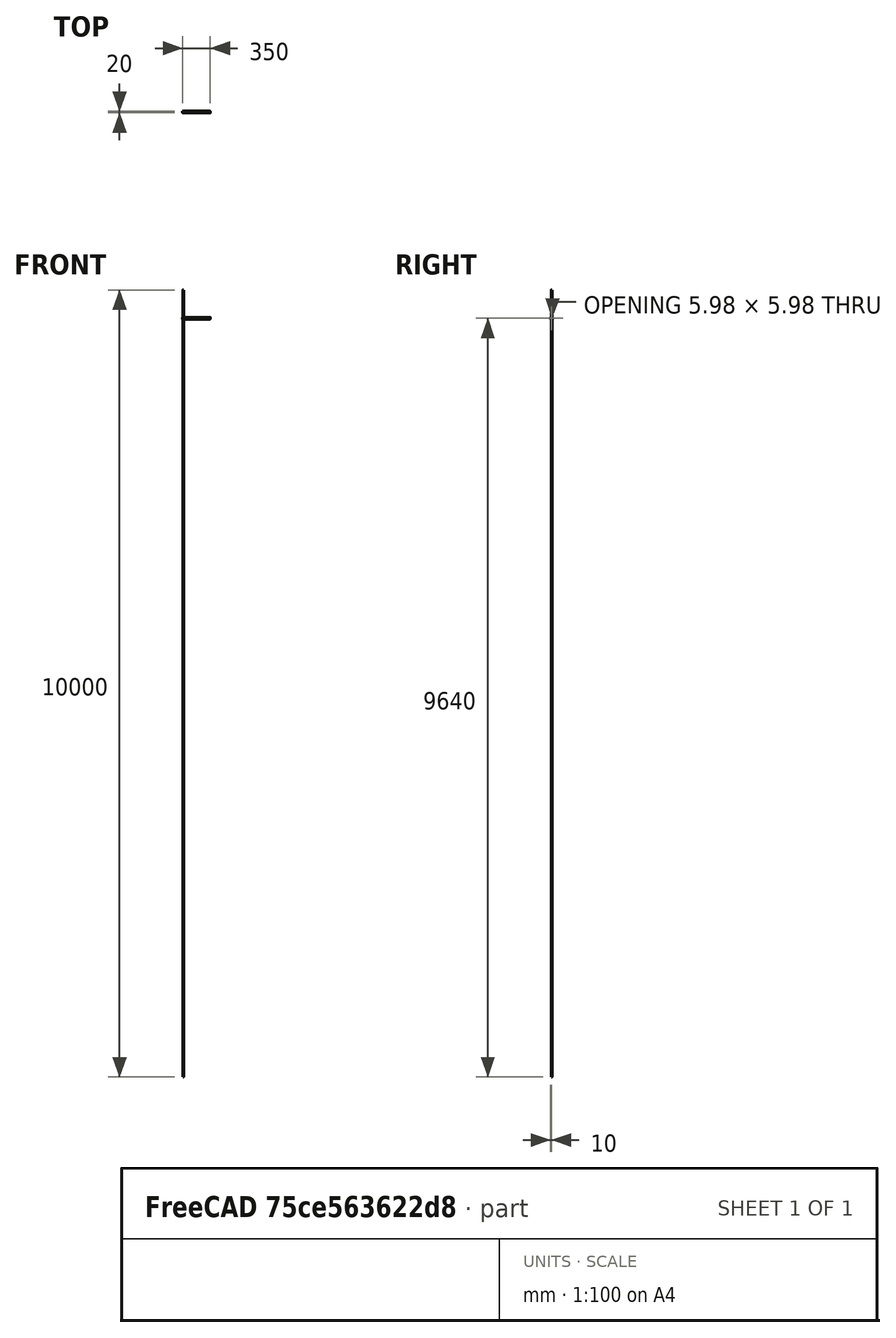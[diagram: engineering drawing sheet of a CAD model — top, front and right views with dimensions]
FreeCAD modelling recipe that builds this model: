
FCSTD DOCUMENT  (FreeCAD 0.14R3703 (Git))
Label: perfiles_horizontales_X
License: CC-BY 3.0
LicenseURL: http://creativecommons.org/licenses/by/3.0/
objects: Sketcher::SketchObject×2, PartDesign::Pad×1, PartDesign::Pocket×1, Part::Feature×1
note: 7 computed .brp shape members not serialized (recipe doc carries the construction recipe); baked Part::Feature solids carry a one-line shape summary decoded from their .brp

FEATURE [Sketcher::SketchObject] Sketch
  Placement = pos=(0,0,-1.5) rot=(0,1,0;1.5708rad)
  sketch-geometry (136):
    g0: LineSegment StartX=0 StartY=20 StartZ=0 EndX=4.65 EndY=20 EndZ=0
    g1: ArcOfCircle CenterX=-1e-12 CenterY=18.5 CenterZ=0 NormalX=0 NormalY=0 NormalZ=1 Radius=1.5 StartAngle=1.5708 EndAngle=3.14159
    g2: LineSegment StartX=-1.5 StartY=13.85 StartZ=0 EndX=-1.5 EndY=18.5 EndZ=0
    g3: ArcOfCircle CenterX=-1.3 CenterY=13.85 CenterZ=0 NormalX=0 NormalY=0 NormalZ=1 Radius=0.2 StartAngle=3.14159 EndAngle=4.71239
    g4: LineSegment StartX=-1 StartY=13.65 StartZ=0 EndX=-1.3 EndY=13.65 EndZ=0
    g5: LineSegment StartX=-1 StartY=13.3 StartZ=0 EndX=-1 EndY=13.65 EndZ=0
    g6: ArcOfCircle CenterX=-0.8 CenterY=13.3 CenterZ=0 NormalX=0 NormalY=0 NormalZ=1 Radius=0.2 StartAngle=3.14159 EndAngle=4.71239
    g7: LineSegment StartX=-0.5 StartY=13.1 StartZ=0 EndX=-0.8 EndY=13.1 EndZ=0
    g8: ArcOfCircle CenterX=-0.5 CenterY=13.6 CenterZ=0 NormalX=0 NormalY=0 NormalZ=1 Radius=0.5 StartAngle=4.71239 EndAngle=6.28319
    g9: LineSegment StartX=2.68e-07 StartY=15.5 StartZ=0 EndX=2.68e-07 EndY=13.6 EndZ=0
    g10: ArcOfCircle CenterX=0.5 CenterY=15.5 CenterZ=0 NormalX=0 NormalY=0 NormalZ=1 Radius=0.5 StartAngle=1.5708 EndAngle=3.14159
    g11: LineSegment StartX=1.23223 StartY=16 StartZ=0 EndX=0.5 EndY=16 EndZ=0
    g12: ArcOfCircle CenterX=1.23223 CenterY=15.5 CenterZ=0 NormalX=0 NormalY=0 NormalZ=1 Radius=0.5 StartAngle=0.785398 EndAngle=1.5708
    g13: LineSegment StartX=3.85355 StartY=13.5858 StartZ=0 EndX=1.58579 EndY=15.8536 EndZ=0
    g14: ArcOfCircle CenterX=3.5 CenterY=13.2322 CenterZ=0 NormalX=0 NormalY=0 NormalZ=1 Radius=0.5 StartAngle=0 EndAngle=0.785398
    g15: LineSegment StartX=4 StartY=10.9536 StartZ=0 EndX=4 EndY=13.2322 EndZ=0
    g16: ArcOfCircle CenterX=4.2 CenterY=10.9536 CenterZ=0 NormalX=0 NormalY=0 NormalZ=1 Radius=0.2 StartAngle=3.14159 EndAngle=3.66519
    g17: LineSegment StartX=4.46188 StartY=10.1 StartZ=0 EndX=4.0268 EndY=10.8536 EndZ=0
    g18: ArcOfCircle CenterX=4.28868 CenterY=10 CenterZ=0 NormalX=0 NormalY=0 NormalZ=1 Radius=0.2 StartAngle=5.75959 EndAngle=6.80678
    g19: LineSegment StartX=4.0268 StartY=9.14641 StartZ=0 EndX=4.46188 EndY=9.9 EndZ=0
    g20: ArcOfCircle CenterX=4.2 CenterY=9.04641 CenterZ=0 NormalX=0 NormalY=0 NormalZ=1 Radius=0.2 StartAngle=2.61799 EndAngle=3.14159
    g21: LineSegment StartX=4 StartY=6.76777 StartZ=0 EndX=4 EndY=9.04641 EndZ=0
    g22: ArcOfCircle CenterX=3.5 CenterY=6.76777 CenterZ=0 NormalX=0 NormalY=0 NormalZ=1 Radius=0.5 StartAngle=5.49779 EndAngle=6.28319
    g23: LineSegment StartX=1.58579 StartY=4.14645 StartZ=0 EndX=3.85355 EndY=6.41421 EndZ=0
    g24: ArcOfCircle CenterX=1.23223 CenterY=4.5 CenterZ=0 NormalX=0 NormalY=0 NormalZ=1 Radius=0.5 StartAngle=4.71239 EndAngle=5.49779
    g25: LineSegment StartX=0.5 StartY=4 StartZ=0 EndX=1.23223 EndY=4 EndZ=0
    g26: ArcOfCircle CenterX=0.5 CenterY=4.5 CenterZ=0 NormalX=0 NormalY=0 NormalZ=1 Radius=0.5 StartAngle=3.14159 EndAngle=4.71239
    g27: LineSegment StartX=2.68e-07 StartY=6.4 StartZ=0 EndX=2.68e-07 EndY=4.5 EndZ=0
    g28: ArcOfCircle CenterX=-0.5 CenterY=6.4 CenterZ=0 NormalX=0 NormalY=0 NormalZ=1 Radius=0.5 StartAngle=0 EndAngle=1.5708
    g29: LineSegment StartX=-0.8 StartY=6.9 StartZ=0 EndX=-0.5 EndY=6.9 EndZ=0
    g30: ArcOfCircle CenterX=-0.8 CenterY=6.7 CenterZ=0 NormalX=0 NormalY=0 NormalZ=1 Radius=0.2 StartAngle=1.5708 EndAngle=3.14159
    g31: LineSegment StartX=-1 StartY=6.35 StartZ=0 EndX=-1 EndY=6.7 EndZ=0
    g32: LineSegment StartX=-1.3 StartY=6.35 StartZ=0 EndX=-1 EndY=6.35 EndZ=0
    g33: ArcOfCircle CenterX=-1.3 CenterY=6.15 CenterZ=0 NormalX=0 NormalY=0 NormalZ=1 Radius=0.2 StartAngle=1.5708 EndAngle=3.14159
    g34: LineSegment StartX=-1.5 StartY=1.5 StartZ=0 EndX=-1.5 EndY=6.15 EndZ=0
    g35: ArcOfCircle CenterX=0 CenterY=1.5 CenterZ=0 NormalX=0 NormalY=0 NormalZ=1 Radius=1.5 StartAngle=3.14159 EndAngle=4.71239
    g36: LineSegment StartX=4.65 StartY=1e-12 StartZ=0 EndX=0 EndY=0 EndZ=0
    g37: ArcOfCircle CenterX=4.65 CenterY=0.2 CenterZ=0 NormalX=0 NormalY=0 NormalZ=1 Radius=0.2 StartAngle=4.71239 EndAngle=6.28319
    g38: LineSegment StartX=4.85 StartY=0.5 StartZ=0 EndX=4.85 EndY=0.2 EndZ=0
    g39: LineSegment StartX=5.2 StartY=0.5 StartZ=0 EndX=4.85 EndY=0.5 EndZ=0
    g40: ArcOfCircle CenterX=5.2 CenterY=0.7 CenterZ=0 NormalX=0 NormalY=0 NormalZ=1 Radius=0.2 StartAngle=4.71239 EndAngle=6.28319
    g41: LineSegment StartX=5.4 StartY=1 StartZ=0 EndX=5.4 EndY=0.7 EndZ=0
    g42: ArcOfCircle CenterX=4.9 CenterY=1 CenterZ=0 NormalX=0 NormalY=0 NormalZ=1 Radius=0.5 StartAngle=0 EndAngle=1.5708
    g43: LineSegment StartX=3 StartY=1.5 StartZ=0 EndX=4.9 EndY=1.5 EndZ=0
    g44: ArcOfCircle CenterX=3 CenterY=2 CenterZ=0 NormalX=0 NormalY=0 NormalZ=1 Radius=0.5 StartAngle=3.14159 EndAngle=4.71239
    g45: LineSegment StartX=2.5 StartY=2.73223 StartZ=0 EndX=2.5 EndY=2 EndZ=0
    g46: ArcOfCircle CenterX=3 CenterY=2.73223 CenterZ=0 NormalX=0 NormalY=0 NormalZ=1 Radius=0.5 StartAngle=2.35619 EndAngle=3.14159
    g47: LineSegment StartX=4.91421 StartY=5.35355 StartZ=0 EndX=2.64645 EndY=3.08579 EndZ=0
    g48: ArcOfCircle CenterX=5.26777 CenterY=5 CenterZ=0 NormalX=0 NormalY=0 NormalZ=1 Radius=0.5 StartAngle=1.5708 EndAngle=2.35619
    g49: LineSegment StartX=7.54641 StartY=5.5 StartZ=0 EndX=5.26777 EndY=5.5 EndZ=0
    g50: ArcOfCircle CenterX=7.54641 CenterY=5.7 CenterZ=0 NormalX=0 NormalY=0 NormalZ=1 Radius=0.2 StartAngle=4.71239 EndAngle=5.23599
    g51: LineSegment StartX=8.4 StartY=5.96188 StartZ=0 EndX=7.64641 EndY=5.52679 EndZ=0
    g52: ArcOfCircle CenterX=8.5 CenterY=5.78868 CenterZ=0 NormalX=0 NormalY=0 NormalZ=1 Radius=0.2 StartAngle=1.0472 EndAngle=2.0944
    g53: LineSegment StartX=9.35359 StartY=5.52679 StartZ=0 EndX=8.6 EndY=5.96188 EndZ=0
    g54: ArcOfCircle CenterX=9.45359 CenterY=5.7 CenterZ=0 NormalX=0 NormalY=0 NormalZ=1 Radius=0.2 StartAngle=4.18879 EndAngle=4.71239
    g55: LineSegment StartX=11.7322 StartY=5.5 StartZ=0 EndX=9.45359 EndY=5.5 EndZ=0
    g56: ArcOfCircle CenterX=11.7322 CenterY=5 CenterZ=0 NormalX=0 NormalY=0 NormalZ=1 Radius=0.5 StartAngle=0.785398 EndAngle=1.5708
    g57: LineSegment StartX=14.3536 StartY=3.08579 StartZ=0 EndX=12.0858 EndY=5.35355 EndZ=0
    g58: ArcOfCircle CenterX=14 CenterY=2.73223 CenterZ=0 NormalX=0 NormalY=0 NormalZ=1 Radius=0.5 StartAngle=0 EndAngle=0.785398
    g59: LineSegment StartX=14.5 StartY=2 StartZ=0 EndX=14.5 EndY=2.73223 EndZ=0
    g60: ArcOfCircle CenterX=14 CenterY=2 CenterZ=0 NormalX=0 NormalY=0 NormalZ=1 Radius=0.5 StartAngle=4.71239 EndAngle=6.28319
    g61: LineSegment StartX=12.1 StartY=1.5 StartZ=0 EndX=14 EndY=1.5 EndZ=0
    g62: ArcOfCircle CenterX=12.1 CenterY=1 CenterZ=0 NormalX=0 NormalY=0 NormalZ=1 Radius=0.5 StartAngle=1.5708 EndAngle=3.14159
    g63: LineSegment StartX=11.6 StartY=0.7 StartZ=0 EndX=11.6 EndY=1 EndZ=0
    g64: ArcOfCircle CenterX=11.8 CenterY=0.7 CenterZ=0 NormalX=0 NormalY=0 NormalZ=1 Radius=0.2 StartAngle=3.14159 EndAngle=4.71239
    g65: LineSegment StartX=12.15 StartY=0.5 StartZ=0 EndX=11.8 EndY=0.5 EndZ=0
    g66: LineSegment StartX=12.15 StartY=0.2 StartZ=0 EndX=12.15 EndY=0.5 EndZ=0
    g67: ArcOfCircle CenterX=12.35 CenterY=0.2 CenterZ=0 NormalX=0 NormalY=0 NormalZ=1 Radius=0.2 StartAngle=3.14159 EndAngle=4.71239
    g68: LineSegment StartX=17 StartY=1e-12 StartZ=0 EndX=12.35 EndY=0 EndZ=0
    g69: ArcOfCircle CenterX=17 CenterY=1.5 CenterZ=0 NormalX=0 NormalY=0 NormalZ=1 Radius=1.5 StartAngle=4.71239 EndAngle=6.28319
    g70: LineSegment StartX=18.5 StartY=6.15 StartZ=0 EndX=18.5 EndY=1.5 EndZ=0
    g71: ArcOfCircle CenterX=18.3 CenterY=6.15 CenterZ=0 NormalX=0 NormalY=0 NormalZ=1 Radius=0.2 StartAngle=0 EndAngle=1.5708
    g72: LineSegment StartX=18 StartY=6.35 StartZ=0 EndX=18.3 EndY=6.35 EndZ=0
    g73: LineSegment StartX=18 StartY=6.7 StartZ=0 EndX=18 EndY=6.35 EndZ=0
    g74: ArcOfCircle CenterX=17.8 CenterY=6.7 CenterZ=0 NormalX=0 NormalY=0 NormalZ=1 Radius=0.2 StartAngle=0 EndAngle=1.5708
    g75: LineSegment StartX=17.5 StartY=6.9 StartZ=0 EndX=17.8 EndY=6.9 EndZ=0
    g76: ArcOfCircle CenterX=17.5 CenterY=6.4 CenterZ=0 NormalX=0 NormalY=0 NormalZ=1 Radius=0.5 StartAngle=1.5708 EndAngle=3.14159
    g77: LineSegment StartX=17 StartY=4.5 StartZ=0 EndX=17 EndY=6.4 EndZ=0
    g78: ArcOfCircle CenterX=16.5 CenterY=4.5 CenterZ=0 NormalX=0 NormalY=0 NormalZ=1 Radius=0.5 StartAngle=4.71239 EndAngle=6.28319
    g79: LineSegment StartX=15.7678 StartY=4 StartZ=0 EndX=16.5 EndY=4 EndZ=0
    g80: ArcOfCircle CenterX=15.7678 CenterY=4.5 CenterZ=0 NormalX=0 NormalY=0 NormalZ=1 Radius=0.5 StartAngle=3.92699 EndAngle=4.71239
    g81: LineSegment StartX=13.1464 StartY=6.41421 StartZ=0 EndX=15.4142 EndY=4.14645 EndZ=0
    g82: ArcOfCircle CenterX=13.5 CenterY=6.76777 CenterZ=0 NormalX=0 NormalY=0 NormalZ=1 Radius=0.5 StartAngle=3.14159 EndAngle=3.92699
    g83: LineSegment StartX=13 StartY=9.04641 StartZ=0 EndX=13 EndY=6.76777 EndZ=0
    g84: ArcOfCircle CenterX=12.8 CenterY=9.04641 CenterZ=0 NormalX=0 NormalY=0 NormalZ=1 Radius=0.2 StartAngle=0 EndAngle=0.523599
    g85: LineSegment StartX=12.5381 StartY=9.9 StartZ=0 EndX=12.9732 EndY=9.14641 EndZ=0
    g86: ArcOfCircle CenterX=12.7113 CenterY=10 CenterZ=0 NormalX=0 NormalY=0 NormalZ=1 Radius=0.2 StartAngle=2.61799 EndAngle=3.66519
    g87: LineSegment StartX=12.9732 StartY=10.8536 StartZ=0 EndX=12.5381 EndY=10.1 EndZ=0
    g88: ArcOfCircle CenterX=12.8 CenterY=10.9536 CenterZ=0 NormalX=0 NormalY=0 NormalZ=1 Radius=0.2 StartAngle=5.75959 EndAngle=6.28319
    g89: LineSegment StartX=13 StartY=13.2322 StartZ=0 EndX=13 EndY=10.9536 EndZ=0
    g90: ArcOfCircle CenterX=13.5 CenterY=13.2322 CenterZ=0 NormalX=0 NormalY=0 NormalZ=1 Radius=0.5 StartAngle=2.35619 EndAngle=3.14159
    g91: LineSegment StartX=15.4142 StartY=15.8536 StartZ=0 EndX=13.1464 EndY=13.5858 EndZ=0
    g92: ArcOfCircle CenterX=15.7678 CenterY=15.5 CenterZ=0 NormalX=0 NormalY=0 NormalZ=1 Radius=0.5 StartAngle=1.5708 EndAngle=2.35619
    g93: LineSegment StartX=16.5 StartY=16 StartZ=0 EndX=15.7678 EndY=16 EndZ=0
    g94: ArcOfCircle CenterX=16.5 CenterY=15.5 CenterZ=0 NormalX=0 NormalY=0 NormalZ=1 Radius=0.5 StartAngle=0 EndAngle=1.5708
    g95: LineSegment StartX=17 StartY=13.6 StartZ=0 EndX=17 EndY=15.5 EndZ=0
    g96: ArcOfCircle CenterX=17.5 CenterY=13.6 CenterZ=0 NormalX=0 NormalY=0 NormalZ=1 Radius=0.5 StartAngle=3.14159 EndAngle=4.71239
    g97: LineSegment StartX=17.8 StartY=13.1 StartZ=0 EndX=17.5 EndY=13.1 EndZ=0
    g98: ArcOfCircle CenterX=17.8 CenterY=13.3 CenterZ=0 NormalX=0 NormalY=0 NormalZ=1 Radius=0.2 StartAngle=4.71239 EndAngle=6.28319
    g99: LineSegment StartX=18 StartY=13.65 StartZ=0 EndX=18 EndY=13.3 EndZ=0
    g100: LineSegment StartX=18.3 StartY=13.65 StartZ=0 EndX=18 EndY=13.65 EndZ=0
    g101: ArcOfCircle CenterX=18.3 CenterY=13.85 CenterZ=0 NormalX=0 NormalY=0 NormalZ=1 Radius=0.2 StartAngle=4.71239 EndAngle=6.28319
    g102: LineSegment StartX=18.5 StartY=18.5 StartZ=0 EndX=18.5 EndY=13.85 EndZ=0
    g103: ArcOfCircle CenterX=17 CenterY=18.5 CenterZ=0 NormalX=0 NormalY=0 NormalZ=1 Radius=1.5 StartAngle=0 EndAngle=1.5708
    g104: LineSegment StartX=12.35 StartY=20 StartZ=0 EndX=17 EndY=20 EndZ=0
    g105: ArcOfCircle CenterX=12.35 CenterY=19.8 CenterZ=0 NormalX=0 NormalY=0 NormalZ=1 Radius=0.2 StartAngle=1.5708 EndAngle=3.14159
    g106: LineSegment StartX=12.15 StartY=19.5 StartZ=0 EndX=12.15 EndY=19.8 EndZ=0
    g107: LineSegment StartX=11.8 StartY=19.5 StartZ=0 EndX=12.15 EndY=19.5 EndZ=0
    g108: ArcOfCircle CenterX=11.8 CenterY=19.3 CenterZ=0 NormalX=0 NormalY=0 NormalZ=1 Radius=0.2 StartAngle=1.5708 EndAngle=3.14159
    g109: LineSegment StartX=11.6 StartY=19 StartZ=0 EndX=11.6 EndY=19.3 EndZ=0
    g110: ArcOfCircle CenterX=12.1 CenterY=19 CenterZ=0 NormalX=0 NormalY=0 NormalZ=1 Radius=0.5 StartAngle=3.14159 EndAngle=4.71239
    g111: LineSegment StartX=14 StartY=18.5 StartZ=0 EndX=12.1 EndY=18.5 EndZ=0
    g112: ArcOfCircle CenterX=14 CenterY=18 CenterZ=0 NormalX=0 NormalY=0 NormalZ=1 Radius=0.5 StartAngle=0 EndAngle=1.5708
    g113: LineSegment StartX=14.5 StartY=17.2678 StartZ=0 EndX=14.5 EndY=18 EndZ=0
    g114: ArcOfCircle CenterX=14 CenterY=17.2678 CenterZ=0 NormalX=0 NormalY=0 NormalZ=1 Radius=0.5 StartAngle=5.49779 EndAngle=6.28319
    g115: LineSegment StartX=12.0858 StartY=14.6464 StartZ=0 EndX=14.3536 EndY=16.9142 EndZ=0
    g116: ArcOfCircle CenterX=11.7322 CenterY=15 CenterZ=0 NormalX=0 NormalY=0 NormalZ=1 Radius=0.5 StartAngle=4.71239 EndAngle=5.49779
    g117: LineSegment StartX=9.45359 StartY=14.5 StartZ=0 EndX=11.7322 EndY=14.5 EndZ=0
    g118: ArcOfCircle CenterX=9.45359 CenterY=14.3 CenterZ=0 NormalX=0 NormalY=0 NormalZ=1 Radius=0.2 StartAngle=1.5708 EndAngle=2.0944
    g119: LineSegment StartX=8.6 StartY=14.0381 StartZ=0 EndX=9.35359 EndY=14.4732 EndZ=0
    g120: ArcOfCircle CenterX=8.5 CenterY=14.2113 CenterZ=0 NormalX=0 NormalY=0 NormalZ=1 Radius=0.2 StartAngle=4.18879 EndAngle=5.23599
    g121: LineSegment StartX=7.64641 StartY=14.4732 StartZ=0 EndX=8.4 EndY=14.0381 EndZ=0
    g122: ArcOfCircle CenterX=7.54641 CenterY=14.3 CenterZ=0 NormalX=0 NormalY=0 NormalZ=1 Radius=0.2 StartAngle=1.0472 EndAngle=1.5708
    g123: LineSegment StartX=5.26777 StartY=14.5 StartZ=0 EndX=7.54641 EndY=14.5 EndZ=0
    g124: ArcOfCircle CenterX=5.26777 CenterY=15 CenterZ=0 NormalX=0 NormalY=0 NormalZ=1 Radius=0.5 StartAngle=3.92699 EndAngle=4.71239
    g125: LineSegment StartX=2.64645 StartY=16.9142 StartZ=0 EndX=4.91421 EndY=14.6464 EndZ=0
    g126: ArcOfCircle CenterX=3 CenterY=17.2678 CenterZ=0 NormalX=0 NormalY=0 NormalZ=1 Radius=0.5 StartAngle=3.14159 EndAngle=3.92699
    g127: LineSegment StartX=2.5 StartY=18 StartZ=0 EndX=2.5 EndY=17.2678 EndZ=0
    g128: ArcOfCircle CenterX=3 CenterY=18 CenterZ=0 NormalX=0 NormalY=0 NormalZ=1 Radius=0.5 StartAngle=1.5708 EndAngle=3.14159
    g129: LineSegment StartX=4.9 StartY=18.5 StartZ=0 EndX=3 EndY=18.5 EndZ=0
    g130: ArcOfCircle CenterX=4.9 CenterY=19 CenterZ=0 NormalX=0 NormalY=0 NormalZ=1 Radius=0.5 StartAngle=4.71239 EndAngle=6.28319
    g131: LineSegment StartX=5.4 StartY=19.3 StartZ=0 EndX=5.4 EndY=19 EndZ=0
    g132: ArcOfCircle CenterX=5.2 CenterY=19.3 CenterZ=0 NormalX=0 NormalY=0 NormalZ=1 Radius=0.2 StartAngle=0 EndAngle=1.5708
    g133: LineSegment StartX=4.85 StartY=19.5 StartZ=0 EndX=5.2 EndY=19.5 EndZ=0
    g134: LineSegment StartX=4.85 StartY=19.8 StartZ=0 EndX=4.85 EndY=19.5 EndZ=0
    g135: ArcOfCircle CenterX=4.65 CenterY=19.8 CenterZ=0 NormalX=0 NormalY=0 NormalZ=1 Radius=0.2 StartAngle=0 EndAngle=1.5708
  constraints (136):
    c: Coincident(g0,g1)
    c: Coincident(g135,g0)
    c: Coincident(g1,g2)
    c: Coincident(g2,g3)
    c: Coincident(g3,g4)
    c: Coincident(g4,g5)
    c: Coincident(g6,g5)
    c: Coincident(g7,g6)
    c: Coincident(g8,g7)
    c: Coincident(g9,g8)
    c: Coincident(g10,g9)
    c: Coincident(g10,g11)
    c: Coincident(g11,g12)
    c: Coincident(g12,g13)
    c: Coincident(g14,g13)
    c: Coincident(g15,g14)
    c: Coincident(g15,g16)
    c: Coincident(g16,g17)
    c: Coincident(g17,g18)
    c: Coincident(g18,g19)
    c: Coincident(g19,g20)
    c: Coincident(g20,g21)
    c: Coincident(g21,g22)
    c: Coincident(g22,g23)
    c: Coincident(g23,g24)
    c: Coincident(g24,g25)
    c: Coincident(g26,g25)
    c: Coincident(g26,g27)
    c: Coincident(g28,g27)
    c: Coincident(g28,g29)
    c: Coincident(g30,g29)
    c: Coincident(g31,g30)
    c: Coincident(g31,g32)
    c: Coincident(g32,g33)
    c: Coincident(g33,g34)
    c: Coincident(g35,g34)
    c: Coincident(g36,g35)
    c: Coincident(g37,g36)
    c: Coincident(g37,g38)
    c: Coincident(g38,g39)
    c: Coincident(g40,g39)
    c: Coincident(g40,g41)
    c: Coincident(g41,g42)
    c: Coincident(g43,g42)
    c: Coincident(g44,g43)
    c: Coincident(g44,g45)
    c: Coincident(g45,g46)
    c: Coincident(g46,g47)
    c: Coincident(g47,g48)
    c: Coincident(g49,g48)
    c: Coincident(g49,g50)
    c: Coincident(g50,g51)
    c: Coincident(g51,g52)
    c: Coincident(g53,g52)
    c: Coincident(g54,g53)
    c: Coincident(g55,g54)
    c: Coincident(g56,g55)
    c: Coincident(g56,g57)
    c: Coincident(g58,g57)
    c: Coincident(g59,g58)
    c: Coincident(g60,g59)
    c: Coincident(g61,g60)
    c: Coincident(g62,g61)
    c: Coincident(g62,g63)
    c: Coincident(g64,g63)
    c: Coincident(g65,g64)
    c: Coincident(g66,g65)
    c: Coincident(g67,g66)
    c: Coincident(g67,g68)
    c: Coincident(g69,g68)
    c: Coincident(g70,g69)
    c: Coincident(g71,g70)
    c: Coincident(g72,g71)
    c: Coincident(g73,g72)
    c: Coincident(g73,g74)
    c: Coincident(g75,g74)
    c: Coincident(g76,g75)
    c: Coincident(g76,g77)
    c: Coincident(g77,g78)
    c: Coincident(g78,g79)
    c: Coincident(g80,g79)
    c: Coincident(g81,g80)
    c: Coincident(g81,g82)
    c: Coincident(g82,g83)
    c: Coincident(g83,g84)
    c: Coincident(g85,g84)
    c: Coincident(g86,g85)
    c: Coincident(g86,g87)
    c: Coincident(g88,g87)
    c: Coincident(g88,g89)
    c: Coincident(g89,g90)
    c: Coincident(g91,g90)
    c: Coincident(g92,g91)
    c: Coincident(g93,g92)
    c: Coincident(g94,g93)
    c: Coincident(g94,g95)
    c: Coincident(g95,g96)
    c: Coincident(g96,g97)
    c: Coincident(g98,g97)
    c: Coincident(g98,g99)
    c: Coincident(g100,g99)
    c: Coincident(g100,g101)
    c: Coincident(g101,g102)
    c: Coincident(g102,g103)
    c: Coincident(g103,g104)
    c: Coincident(g104,g105)
    c: Coincident(g106,g105)
    c: Coincident(g107,g106)
    c: Coincident(g108,g107)
    c: Coincident(g109,g108)
    c: Coincident(g110,g109)
    c: Coincident(g111,g110)
    c: Coincident(g112,g111)
    c: Coincident(g112,g113)
    c: Coincident(g113,g114)
    c: Coincident(g114,g115)
    c: Coincident(g115,g116)
    c: Coincident(g117,g116)
    c: Coincident(g118,g117)
    c: Coincident(g119,g118)
    c: Coincident(g119,g120)
    c: Coincident(g121,g120)
    c: Coincident(g121,g122)
    c: Coincident(g122,g123)
    c: Coincident(g124,g123)
    c: Coincident(g124,g125)
    c: Coincident(g126,g125)
    c: Coincident(g127,g126)
    c: Coincident(g128,g127)
    c: Coincident(g129,g128)
    c: Coincident(g130,g129)
    c: Coincident(g130,g131)
    c: Coincident(g131,g132)
    c: Coincident(g133,g132)
    c: Coincident(g134,g133)
    c: Coincident(g135,g134)
FEATURE [PartDesign::Pad] Pad
  Length = 350
  Length2 = 100
  Placement = pos=(0,0,-1.5) rot=(0,1,0;1.5708rad)
  Sketch = -> Sketch
  Type = 0
FEATURE [Sketcher::SketchObject] Sketch001
  Placement = pos=(350,0,-1.5) rot=(0,1,0;1.5708rad)
  Support = -> Pad [Face138]
  sketch-geometry (16):
    g0: ArcOfCircle CenterX=8.5 CenterY=10 CenterZ=0 NormalX=0 NormalY=0 NormalZ=1 Radius=3.54978 StartAngle=2.14023 EndAngle=2.57348
    g1: LineSegment StartX=6.5861 StartY=12.9896 StartZ=0 EndX=7.24181 EndY=12.4453 EndZ=0
    g2: ArcOfCircle CenterX=8.5 CenterY=10 CenterZ=0 NormalX=0 NormalY=0 NormalZ=1 Radius=2.75 StartAngle=1.09559 EndAngle=2.046
    g3: LineSegment StartX=9.75819 StartY=12.4453 StartZ=0 EndX=10.4139 EndY=12.9896 EndZ=0
    g4: ArcOfCircle CenterX=8.5 CenterY=10 CenterZ=0 NormalX=0 NormalY=0 NormalZ=1 Radius=3.54978 StartAngle=0.568112 EndAngle=1.00136
    g5: LineSegment StartX=11.4922 StartY=11.9099 StartZ=0 EndX=10.9453 EndY=11.2582 EndZ=0
    g6: ArcOfCircle CenterX=8.5 CenterY=10 CenterZ=0 NormalX=0 NormalY=0 NormalZ=1 Radius=2.75 StartAngle=5.80798 EndAngle=6.75839
    g7: LineSegment StartX=10.9453 StartY=8.74181 StartZ=0 EndX=11.4922 EndY=8.09007 EndZ=0
    g8: ArcOfCircle CenterX=8.5 CenterY=10 CenterZ=0 NormalX=0 NormalY=0 NormalZ=1 Radius=3.54978 StartAngle=5.28183 EndAngle=5.71507
    g9: LineSegment StartX=10.4139 StartY=7.01036 StartZ=0 EndX=9.75819 EndY=7.5547 EndZ=0
    g10: ArcOfCircle CenterX=8.5 CenterY=10 CenterZ=0 NormalX=0 NormalY=0 NormalZ=1 Radius=2.75 StartAngle=4.23718 EndAngle=5.1876
    g11: LineSegment StartX=7.24181 StartY=7.5547 StartZ=0 EndX=6.5861 EndY=7.01036 EndZ=0
    g12: ArcOfCircle CenterX=8.5 CenterY=10 CenterZ=0 NormalX=0 NormalY=0 NormalZ=1 Radius=3.54978 StartAngle=3.7097 EndAngle=4.14295
    g13: LineSegment StartX=5.50783 StartY=8.09007 StartZ=0 EndX=6.0547 EndY=8.74181 EndZ=0
    g14: ArcOfCircle CenterX=8.5 CenterY=10 CenterZ=0 NormalX=0 NormalY=0 NormalZ=1 Radius=2.75 StartAngle=2.66639 EndAngle=3.6168
    g15: LineSegment StartX=6.0547 StartY=11.2582 StartZ=0 EndX=5.50783 EndY=11.9099 EndZ=0
  constraints (16):
    c: Coincident(g0,g1)
    c: Coincident(g15,g0)
    c: Coincident(g1,g2)
    c: Coincident(g3,g2)
    c: Coincident(g4,g3)
    c: Coincident(g4,g5)
    c: Coincident(g6,g5)
    c: Coincident(g7,g6)
    c: Coincident(g8,g7)
    c: Coincident(g9,g8)
    c: Coincident(g10,g9)
    c: Coincident(g11,g10)
    c: Coincident(g12,g11)
    c: Coincident(g13,g12)
    c: Coincident(g14,g13)
    c: Coincident(g15,g14)
FEATURE [PartDesign::Pocket] Pocket
  Length = 5
  Placement = pos=(0,0,-1.5) rot=(0,1,0;1.5708rad)
  Sketch = -> Sketch001
  Type = 1
FEATURE [Part::Feature] Pocket001  label="perfiles_horizontales_X"
  Placement = pos=(0,0,-1.5) rot=(0,1,0;1.5708rad)
  shape: bbox 350 x 20 x 20 mm, 154 faces (baked)
